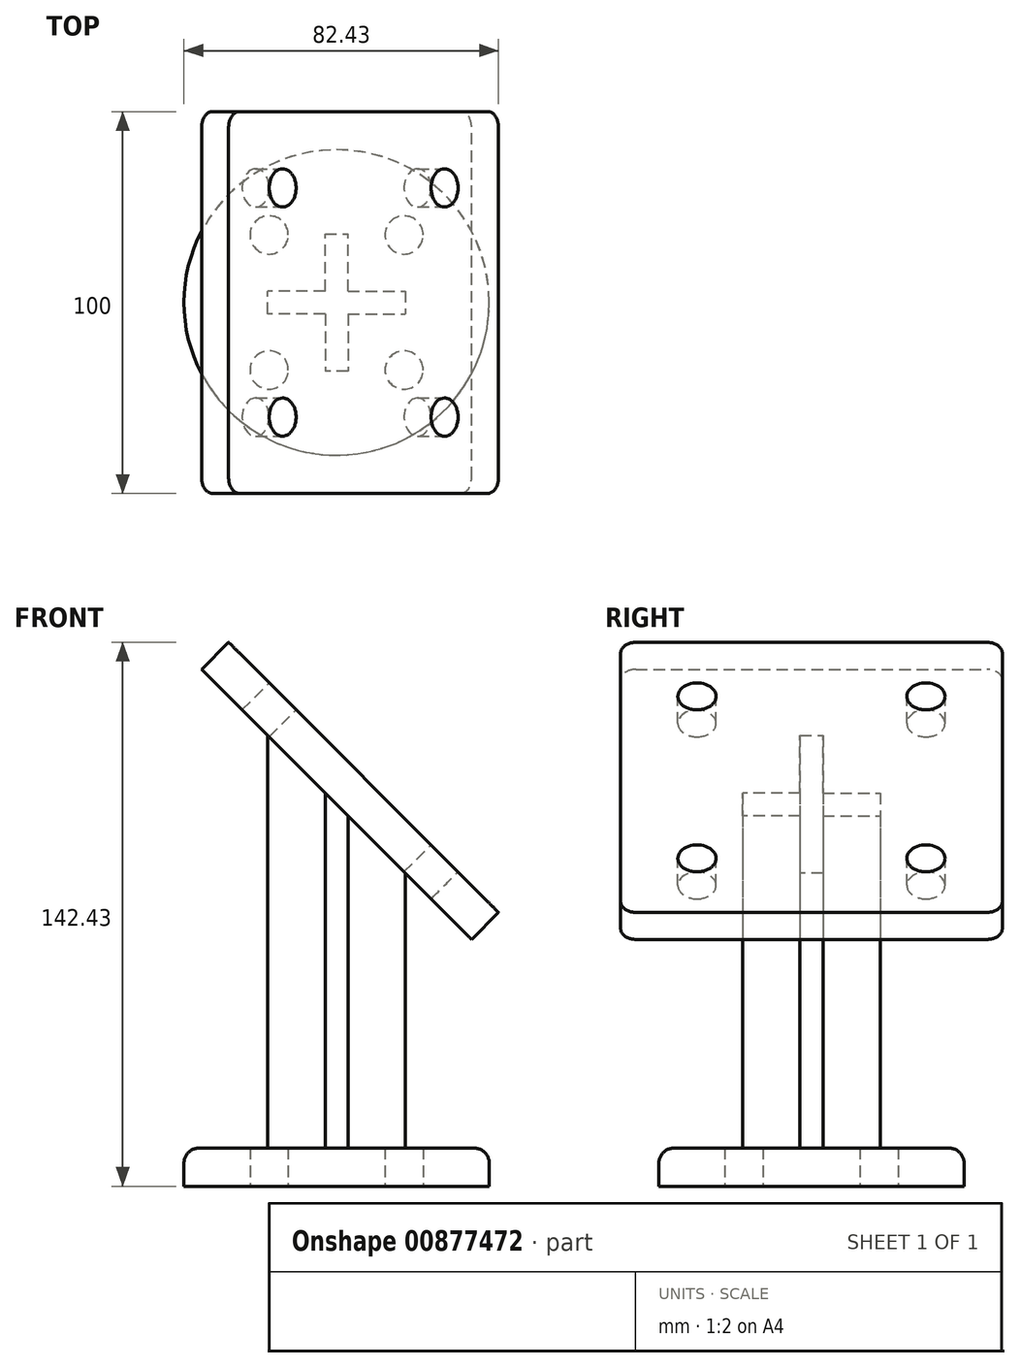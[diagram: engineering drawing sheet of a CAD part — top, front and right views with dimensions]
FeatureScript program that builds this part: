
annotation { "Feature Type Name" : "Feature", "Feature Type Description" : "" }
export const myFeature = defineFeature(function(context is Context, id is Id, definition is map)
    precondition{}
    {
        {
            var Q0;
            Q0=qCreatedBy(makeId("Top.planeOp"),FACE);
            var sketch = newSketch(context, id + "F0", { "sketchPlane" : qUnion([Q0])});
            skCircle(sketch, "E0", {"center": v(0, 0) * mm, "radius": 40 * mm});
            skCircle(sketch, "E1", {"center": v(0, 0) * mm, "radius": 25 * mm, "construction": true});
            skLineSegment(sketch, "E2", {"start": v(0, 0) * mm, "end": v(0, 25) * mm, "construction": true});
            skLineSegment(sketch, "E3", {"start": v(0, 0) * mm, "end": v(17.68, 17.68) * mm, "construction": true});
            skCircle(sketch, "E4", {"center": v(17.68, 17.68) * mm, "radius": 5 * mm});
            skCircle(sketch, "E5.1.0", {"center": v(-17.68, 17.68) * mm, "radius": 5 * mm});
            skCircle(sketch, "E5.2.0", {"center": v(-17.68, -17.68) * mm, "radius": 5 * mm});
            skCircle(sketch, "E5.3.0", {"center": v(17.68, -17.68) * mm, "radius": 5 * mm});
            skSolve(sketch);
        }
        {
            var Q0;
            Q0 = qSketchRegion(id + "F0", true);
            extrude(context, id + "F1", {"entities" : qUnion([Q0]), "depth" : 10 * mm, "offsetDistance" : 25 * mm});
        }
        {
            var Q0;
            Q0=qCreatedBy(makeId("Front.planeOp"),FACE);
            var sketch = newSketch(context, id + "F2", { "sketchPlane" : qUnion([Q0])});
            skLineSegment(sketch, "E6.bottom", {"start": v(-28.28, 142.43) * mm, "end": v(42.43, 71.72) * mm});
            skLineSegment(sketch, "E6.top", {"start": v(-35.36, 135.36) * mm, "end": v(35.36, 64.64) * mm});
            skLineSegment(sketch, "E6.left", {"start": v(-28.28, 142.43) * mm, "end": v(-35.36, 135.36) * mm});
            skLineSegment(sketch, "E6.right", {"start": v(42.43, 71.72) * mm, "end": v(35.36, 64.64) * mm});
            skLineSegment(sketch, "E7", {"start": v(0, 0) * mm, "end": v(0, 100) * mm, "construction": true});
            skSolve(sketch);
        }
        {
            var Q0;
            Q0 = qSketchRegion(id + "F2", true);
            extrude(context, id + "F3", {"entities" : qUnion([Q0]), "endBound" : BoundingType.SYMMETRIC, "depth" : 100 * mm, "offsetDistance" : 25 * mm});
        }
        {
            var Q0;
            Q0=makeQuery(id+"F3.opExtrude","SWEPT_FACE",FACE,{"disambiguationData":[OSD([sQuery(id+"F2.wireOp",EDGE,"E6.bottom")])]});
            var sketch = newSketch(context, id + "F4", { "sketchPlane" : qUnion([Q0])});
            skCircle(sketch, "E8", {"center": v(-30, 100.71) * mm, "radius": 5 * mm});
            skLineSegment(sketch, "E9", {"start": v(-50, 70.71) * mm, "end": v(50, 70.71) * mm, "construction": true});
            skLineSegment(sketch, "E10", {"start": v(0, 120.71) * mm, "end": v(0, 20.71) * mm, "construction": true});
            skCircle(sketch, "E11.MirrorC", {"center": v(-30, 40.71) * mm, "radius": 5 * mm});
            skCircle(sketch, "E12.MirrorC", {"center": v(30, 100.71) * mm, "radius": 5 * mm});
            skCircle(sketch, "E13.MirrorC", {"center": v(30, 40.71) * mm, "radius": 5 * mm});
            skSolve(sketch);
        }
        {
            var Q0;
            Q0 = qSketchRegion(id + "F4", true);
            extrude(context, id + "F5", {"entities" : qUnion([Q0]), "operationType" : NewBodyOperationType.REMOVE, "oppositeDirection" : true, "depth" : 25 * mm, "offsetDistance" : 25 * mm});
        }
        {
            var Q0;
            Q0=makeQuery(id+"F1.opExtrude","CAP_FACE",FACE,{"disambiguationData":[OSD([sQuery(id+"F0.wireOp",EDGE,"E0"),sQuery(id+"F0.wireOp",EDGE,"E4"),sQuery(id+"F0.wireOp",EDGE,"E5.1.0"),sQuery(id+"F0.wireOp",EDGE,"E5.2.0"),sQuery(id+"F0.wireOp",EDGE,"E5.3.0")])],"isStart":false});
            var sketch = newSketch(context, id + "F6", { "sketchPlane" : qUnion([Q0])});
            skLineSegment(sketch, "E14", {"start": v(0, 0) * mm, "end": v(-40, 0) * mm, "construction": true});
            skLineSegment(sketch, "E15", {"start": v(-3, 3) * mm, "end": v(-18, 3) * mm});
            skLineSegment(sketch, "E16.MirrorCS", {"start": v(-3, -3) * mm, "end": v(-18, -3) * mm});
            skLineSegment(sketch, "E17", {"start": v(-18, -3) * mm, "end": v(-18, 3) * mm});
            skLineSegment(sketch, "E18.1.0", {"start": v(3, -3) * mm, "end": v(3, -18) * mm});
            skLineSegment(sketch, "E18.1.1", {"start": v(3, -18) * mm, "end": v(-3, -18) * mm});
            skLineSegment(sketch, "E18.1.2", {"start": v(-3, -3) * mm, "end": v(-3, -18) * mm});
            skLineSegment(sketch, "E18.2.0", {"start": v(3, 3) * mm, "end": v(18, 3) * mm});
            skLineSegment(sketch, "E18.2.1", {"start": v(18, 3) * mm, "end": v(18, -3) * mm});
            skLineSegment(sketch, "E18.2.2", {"start": v(3, -3) * mm, "end": v(18, -3) * mm});
            skLineSegment(sketch, "E18.3.0", {"start": v(-3, 3) * mm, "end": v(-3, 18) * mm});
            skLineSegment(sketch, "E18.3.1", {"start": v(-3, 18) * mm, "end": v(3, 18) * mm});
            skLineSegment(sketch, "E18.3.2", {"start": v(3, 3) * mm, "end": v(3, 18) * mm});
            skPoint(sketch, "E18.center", {"position": v(0, 0) * mm});
            skPoint(sketch, "E19.orphan", {"position": v(0, -3) * mm});
            skPoint(sketch, "E20.orphan", {"position": v(-3, 0) * mm});
            skPoint(sketch, "E21.orphan", {"position": v(0, 3) * mm});
            skPoint(sketch, "E22.orphan", {"position": v(3, 0) * mm});
            skSolve(sketch);
        }
        {
            var Q0;
            Q0 = qSketchRegion(id + "F6", true);
            extrude(context, id + "F7", {"entities" : qUnion([Q0]), "endBound" : BoundingType.UP_TO_NEXT, "depth" : 25 * mm, "offsetDistance" : 25 * mm});
        }
        {
            var Q0;
            Q0=makeQuery(id+"F1.opExtrude","CAP_EDGE",EDGE,{"disambiguationData":[OSD([sQuery(id+"F0.wireOp",EDGE,"E0")])],"isStart":false});
            var Q1;
            Q1=makeQuery(id+"F3.opExtrude","CAP_EDGE",EDGE,{"disambiguationData":[OSD([sQuery(id+"F2.wireOp",EDGE,"E6.right")])],"isStart":false});
            var Q2;
            Q2=makeQuery(id+"F3.opExtrude","CAP_EDGE",EDGE,{"disambiguationData":[OSD([sQuery(id+"F2.wireOp",EDGE,"E6.left")])],"isStart":false});
            var Q3;
            Q3=makeQuery(id+"F3.opExtrude","CAP_EDGE",EDGE,{"disambiguationData":[OSD([sQuery(id+"F2.wireOp",EDGE,"E6.left")])],"isStart":true});
            var Q4;
            Q4=makeQuery(id+"F3.opExtrude","CAP_EDGE",EDGE,{"disambiguationData":[OSD([sQuery(id+"F2.wireOp",EDGE,"E6.right")])],"isStart":true});
            fillet(context, id + "F8", {"entities" : qUnion([Q0, Q1, Q2, Q3, Q4]), "radius" : 4 * mm, "tangentPropagation" : true, "allowEdgeOverflow" : false});
        }
    });
